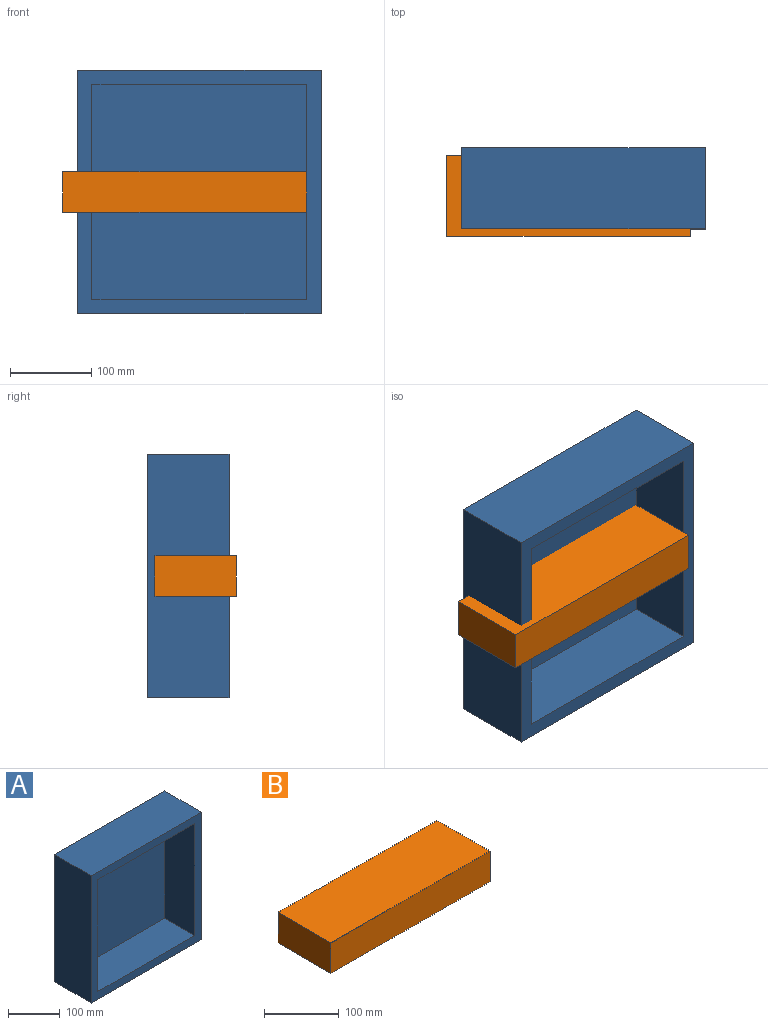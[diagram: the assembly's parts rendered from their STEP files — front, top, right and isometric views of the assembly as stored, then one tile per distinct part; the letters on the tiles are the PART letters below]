
ASSEMBLY  parts=2 mates=1
PART A: 11 faces, bbox 300x100x300 mm
  f0: plane 300x300mm, normal (0,-1,0), area 20304mm2, adj f1,f2,f3,f4,f6,f7,f8,f9
  f1: plane 300x100mm, normal (0,0,1), area 30000mm2, adj f0,f2,f4,f5
  f2: plane 300x100mm, normal (-1,0,0), area 30000mm2, adj f0,f1,f3,f5
  f3: plane 300x100mm, normal (0,0,-1), area 30000mm2, adj f0,f2,f4,f5
  f4: plane 300x100mm, normal (1,0,0), area 30000mm2, adj f0,f1,f3,f5
  f5: plane 300x300mm, normal (0,1,0), area 90000mm2, adj f1,f2,f3,f4
  f6: plane 264x82mm, normal (0,0,-1), area 21648mm2, adj f0,f7,f9,f10
  f7: plane 264x82mm, normal (1,0,0), area 21648mm2, adj f0,f6,f8,f10
  f8: plane 264x82mm, normal (0,0,1), area 21648mm2, adj f0,f7,f9,f10
  f9: plane 264x82mm, normal (-1,0,0), area 21648mm2, adj f0,f6,f8,f10
  f10: plane 264x264mm, normal (0,-1,0), area 69696mm2, adj f6,f7,f8,f9
PART B: 6 faces, bbox 300x100x50 mm
  f0: plane 300x100mm, normal (0,0,1), area 30000mm2, adj f1,f3,f4,f5
  f1: plane 100x50mm, normal (-1,0,0), area 5000mm2, adj f0,f2,f4,f5
  f2: plane 300x100mm, normal (0,0,-1), area 30000mm2, adj f1,f3,f4,f5
  f3: plane 100x50mm, normal (1,0,0), area 5000mm2, adj f0,f2,f4,f5
  f4: plane 300x50mm, normal (0,-1,0), area 15000mm2, adj f0,f1,f2,f3
  f5: plane 300x50mm, normal (0,1,0), area 15000mm2, adj f0,f1,f2,f3
PLACE A t=(145.89,32.35,-25.86)mm
PLACE B t=(131.62,23.35,47.81)mm
MATE fastened B.f3 <-> A.f9  axis (1,0,0) through (276.55,-26.65,56.27)mm
